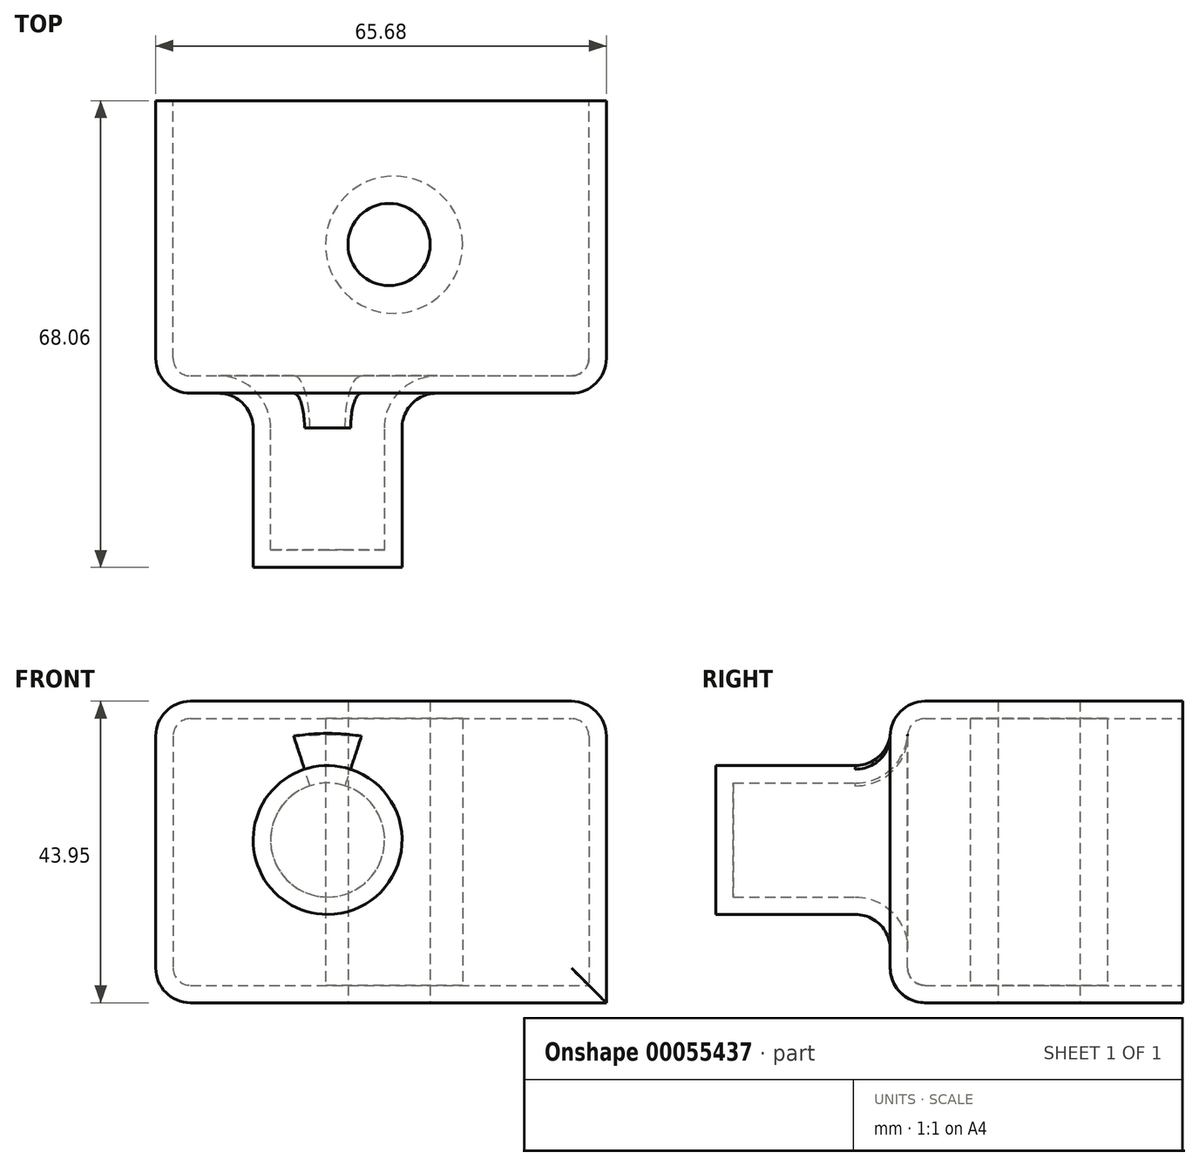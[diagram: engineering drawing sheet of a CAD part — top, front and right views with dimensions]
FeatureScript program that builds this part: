
annotation { "Feature Type Name" : "Feature", "Feature Type Description" : "" }
export const myFeature = defineFeature(function(context is Context, id is Id, definition is map)
    precondition{}
    {
        {
            var Q0;
            Q0=qCreatedBy(makeId("Front.planeOp"),FACE);
            var sketch = newSketch(context, id + "F0", { "sketchPlane" : qUnion([Q0])});
            skLineSegment(sketch, "E0.bottom", {"start": v(0, 0) * mm, "end": v(65.68, 0) * mm});
            skLineSegment(sketch, "E0.top", {"start": v(0, -43.95) * mm, "end": v(65.68, -43.95) * mm});
            skLineSegment(sketch, "E0.left", {"start": v(0, 0) * mm, "end": v(0, -43.95) * mm});
            skLineSegment(sketch, "E0.right", {"start": v(65.68, 0) * mm, "end": v(65.68, -43.95) * mm});
            skSolve(sketch);
        }
        {
            var Q0;
            Q0 = qSketchRegion(id + "F0", true);
            extrude(context, id + "F1", {"entities" : qUnion([Q0]), "depth" : 42.66 * mm});
        }
        {
            var Q0;
            Q0=makeQuery(id+"F1.opExtrude","CAP_FACE",FACE,{"disambiguationData":[OSD([sQuery(id+"F0.wireOp",EDGE,"E0.bottom"),sQuery(id+"F0.wireOp",EDGE,"E0.top"),sQuery(id+"F0.wireOp",EDGE,"E0.left"),sQuery(id+"F0.wireOp",EDGE,"E0.right")])],"isStart":false});
            var sketch = newSketch(context, id + "F2", { "sketchPlane" : qUnion([Q0])});
            skCircle(sketch, "E1", {"center": v(25.06, -20.23) * mm, "radius": 10.85 * mm});
            skSolve(sketch);
        }
        {
            var Q0;
            Q0 = qSketchRegion(id + "F2", true);
            extrude(context, id + "F3", {"entities" : qUnion([Q0]), "operationType" : NewBodyOperationType.ADD, "depth" : 25.4 * mm});
        }
        {
            var Q0;
            Q0=makeQuery(id+"F1.opExtrude","CAP_EDGE",EDGE,{"disambiguationData":[OSD([sQuery(id+"F0.wireOp",EDGE,"E0.right")])],"isStart":false});
            var Q1;
            Q1=makeQuery(id+"F1.opExtrude","CAP_EDGE",EDGE,{"disambiguationData":[OSD([sQuery(id+"F0.wireOp",EDGE,"E0.bottom")])],"isStart":false});
            var Q2;
            Q2=makeQuery(id+"F1.opExtrude","CAP_EDGE",EDGE,{"disambiguationData":[OSD([sQuery(id+"F0.wireOp",EDGE,"E0.left")])],"isStart":false});
            var Q3;
            Q3=makeQuery(id+"F1.opExtrude","CAP_EDGE",EDGE,{"disambiguationData":[OSD([sQuery(id+"F0.wireOp",EDGE,"E0.top")])],"isStart":false});
            var Q4;
            Q4=makeQuery(id+"F1.opExtrude","SWEPT_EDGE",EDGE,{"disambiguationData":[OSD([sQuery(id+"F0.wireOp",EDGE,"E0.bottom"),sQuery(id+"F0.wireOp",EDGE,"E0.right")])]});
            var Q5;
            Q5=makeQuery(id+"F1.opExtrude","SWEPT_EDGE",EDGE,{"disambiguationData":[OSD([sQuery(id+"F0.wireOp",EDGE,"E0.bottom"),sQuery(id+"F0.wireOp",EDGE,"E0.left")])]});
            var Q6;
            Q6=makeQuery(id+"F1.opExtrude","SWEPT_EDGE",EDGE,{"disambiguationData":[OSD([sQuery(id+"F0.wireOp",EDGE,"E0.top"),sQuery(id+"F0.wireOp",EDGE,"E0.left")])]});
            fillet(context, id + "F4", {"entities" : qUnion([Q0, Q1, Q2, Q3, Q4, Q5, Q6]), "radius" : 5.08 * mm, "tangentPropagation" : true, "allowEdgeOverflow" : false});
        }
        {
            var Q0;
            Q0=makeQuery(id+"F1.opExtrude","CAP_FACE",FACE,{"disambiguationData":[OSD([sQuery(id+"F0.wireOp",EDGE,"E0.bottom"),sQuery(id+"F0.wireOp",EDGE,"E0.top"),sQuery(id+"F0.wireOp",EDGE,"E0.left"),sQuery(id+"F0.wireOp",EDGE,"E0.right")])],"isStart":false});
            fillet(context, id + "F5", {"entities" : qUnion([Q0]), "radius" : 5.08 * mm, "tangentPropagation" : true, "allowEdgeOverflow" : false});
        }
        {
            var Q0;
            Q0=makeQuery(id+"F1.opExtrude","CAP_FACE",FACE,{"disambiguationData":[OSD([sQuery(id+"F0.wireOp",EDGE,"E0.bottom"),sQuery(id+"F0.wireOp",EDGE,"E0.top"),sQuery(id+"F0.wireOp",EDGE,"E0.left"),sQuery(id+"F0.wireOp",EDGE,"E0.right")])],"isStart":true});
            shell(context, id + "F6", {"entities" : qUnion([Q0]), "thickness" : 2.54 * mm});
        }
        {
            var Q0;
            Q0=makeQuery(id+"F1.opExtrude","SWEPT_FACE",FACE,{"disambiguationData":[OSD([sQuery(id+"F0.wireOp",EDGE,"E0.top")])]});
            var sketch = newSketch(context, id + "F7", { "sketchPlane" : qUnion([Q0])});
            skCircle(sketch, "E2", {"center": v(34.74, 21) * mm, "radius": 10 * mm});
            skSolve(sketch);
        }
        {
            var Q0;
            Q0 = qSketchRegion(id + "F7", true);
            var Q1;
            Q1=makeQuery(id+"F1.opExtrude","SWEPT_FACE",FACE,{"disambiguationData":[OSD([sQuery(id+"F0.wireOp",EDGE,"E0.bottom")])]});
            extrude(context, id + "F8", {"entities" : qUnion([Q0]), "operationType" : NewBodyOperationType.ADD, "endBound" : BoundingType.UP_TO_SURFACE, "oppositeDirection" : true, "endBoundEntityFace" : qUnion([Q1]), "depth" : 25.4 * mm});
        }
        {
            var Q0;
            Q0=makeQuery(id+"F1.opExtrude","SWEPT_FACE",FACE,{"disambiguationData":[OSD([sQuery(id+"F0.wireOp",EDGE,"E0.top")])]});
            var sketch = newSketch(context, id + "F9", { "sketchPlane" : qUnion([Q0])});
            skCircle(sketch, "E3", {"center": v(34.02, 20.98) * mm, "radius": 6 * mm});
            skSolve(sketch);
        }
        {
            var Q0;
            Q0 = qSketchRegion(id + "F9", true);
            extrude(context, id + "F10", {"entities" : qUnion([Q0]), "operationType" : NewBodyOperationType.REMOVE, "oppositeDirection" : true, "depth" : 65.6 * mm});
        }
    });
